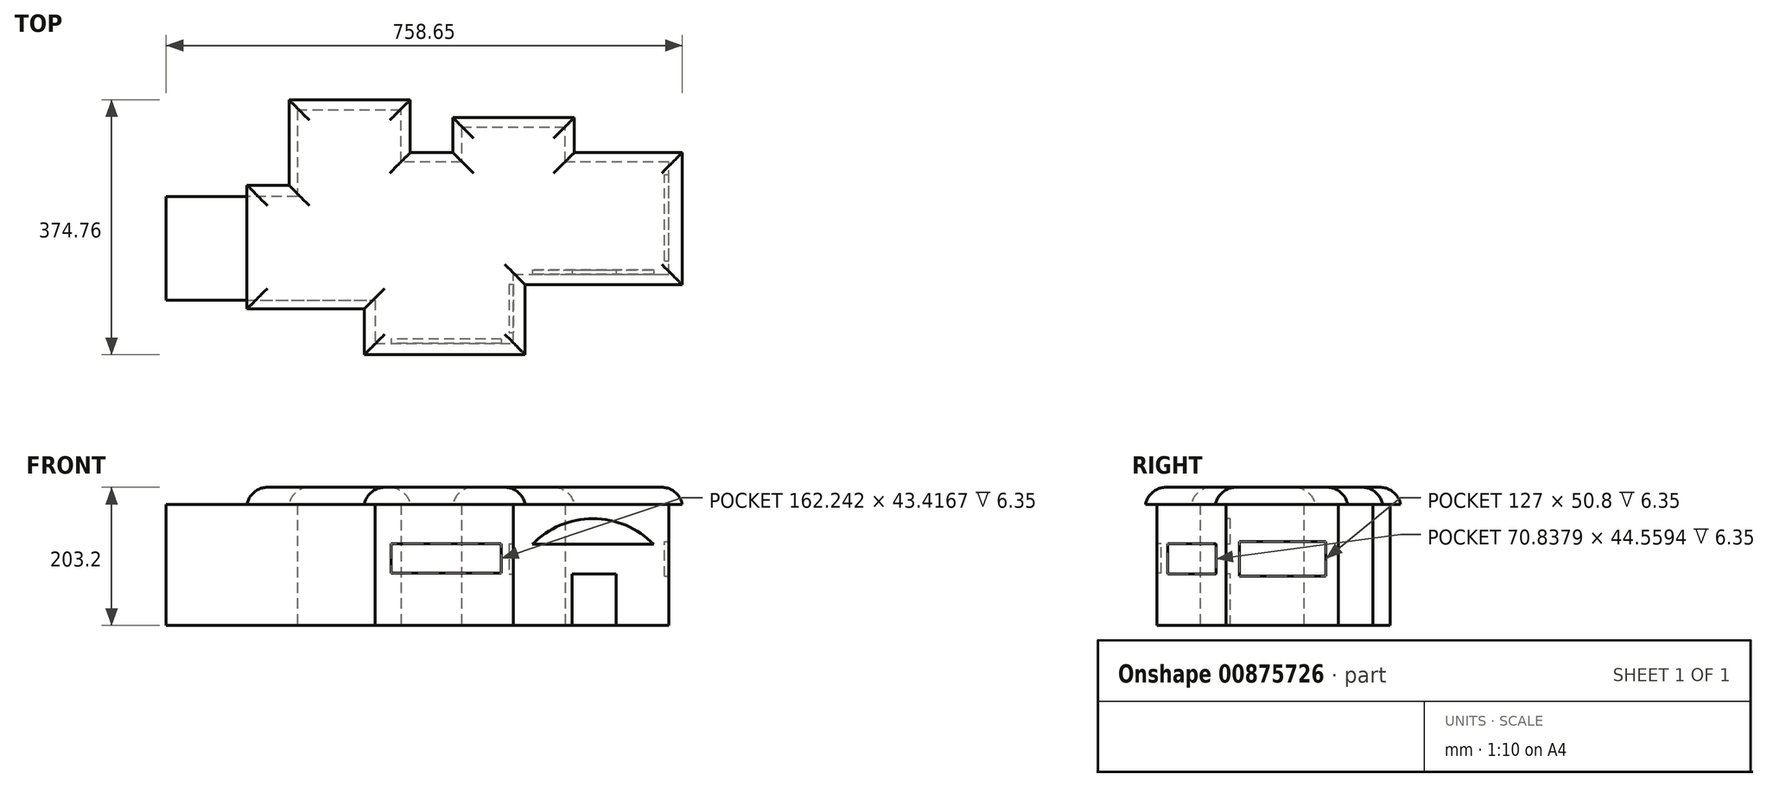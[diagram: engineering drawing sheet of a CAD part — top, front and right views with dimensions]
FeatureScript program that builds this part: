
annotation { "Feature Type Name" : "Feature", "Feature Type Description" : "" }
export const myFeature = defineFeature(function(context is Context, id is Id, definition is map)
    precondition{}
    {
        {
            var Q0;
            Q0=qCreatedBy(makeId("Top.planeOp"),FACE);
            var sketch = newSketch(context, id + "F0", { "sketchPlane" : qUnion([Q0])});
            skLineSegment(sketch, "E0", {"start": v(285.95, -165.1) * mm, "end": v(285.95, 0) * mm});
            skLineSegment(sketch, "E1", {"start": v(285.95, 0) * mm, "end": v(133.55, 0) * mm});
            skLineSegment(sketch, "E2", {"start": v(133.55, 0) * mm, "end": v(133.55, 50.8) * mm});
            skLineSegment(sketch, "E3", {"start": v(133.55, 50.8) * mm, "end": v(-18.85, 50.8) * mm});
            skLineSegment(sketch, "E4", {"start": v(-18.85, 50.8) * mm, "end": v(-18.85, 0) * mm});
            skLineSegment(sketch, "E5", {"start": v(-18.85, 0) * mm, "end": v(-107.75, 0) * mm});
            skLineSegment(sketch, "E6", {"start": v(-107.75, 0) * mm, "end": v(-107.75, 76.2) * mm});
            skLineSegment(sketch, "E7", {"start": v(-107.75, 76.2) * mm, "end": v(-260.15, 76.2) * mm});
            skLineSegment(sketch, "E8", {"start": v(-260.15, 76.2) * mm, "end": v(-260.15, -50.8) * mm});
            skLineSegment(sketch, "E9", {"start": v(-260.15, -50.8) * mm, "end": v(-310.95, -50.8) * mm});
            skLineSegment(sketch, "E10", {"start": v(-310.95, -50.8) * mm, "end": v(-310.95, -203.2) * mm});
            skLineSegment(sketch, "E11", {"start": v(-310.95, -203.2) * mm, "end": v(-145.85, -203.2) * mm});
            skLineSegment(sketch, "E12", {"start": v(-145.85, -203.2) * mm, "end": v(-145.85, -266.7) * mm});
            skLineSegment(sketch, "E13", {"start": v(-145.85, -266.7) * mm, "end": v(57.35, -266.7) * mm});
            skLineSegment(sketch, "E14", {"start": v(57.35, -266.7) * mm, "end": v(57.35, -165.1) * mm});
            skLineSegment(sketch, "E15", {"start": v(57.35, -165.1) * mm, "end": v(285.95, -165.1) * mm});
            skSolve(sketch);
        }
        {
            var Q0;
            Q0 = qSketchRegion(id + "F0", true);
            extrude(context, id + "F1", {"entities" : qUnion([Q0]), "depth" : 177.8 * mm, "offsetDistance" : 25.4 * mm});
        }
        {
            var Q0;
            Q0=makeQuery(id+"F1.opExtrude","SWEPT_FACE",FACE,{"disambiguationData":[OSD([sQuery(id+"F0.wireOp",EDGE,"E15")])]});
            var sketch = newSketch(context, id + "F2", { "sketchPlane" : qUnion([Q0])});
            skLineSegment(sketch, "E16", {"start": v(143.66, 0) * mm, "end": v(143.66, 75.76) * mm});
            skLineSegment(sketch, "E17", {"start": v(143.66, 75.76) * mm, "end": v(208.79, 75.76) * mm});
            skLineSegment(sketch, "E18", {"start": v(208.79, 75.76) * mm, "end": v(208.79, 0) * mm});
            skLineSegment(sketch, "E19", {"start": v(208.79, 0) * mm, "end": v(143.66, 0) * mm});
            skSolve(sketch);
        }
        {
            var Q0;
            Q0 = qSketchRegion(id + "F2", true);
            extrude(context, id + "F3", {"entities" : qUnion([Q0]), "operationType" : NewBodyOperationType.REMOVE, "oppositeDirection" : true, "depth" : 6.35 * mm, "offsetDistance" : 25.4 * mm});
        }
        {
            var Q0;
            Q0=makeQuery(id+"F1.opExtrude","SWEPT_FACE",FACE,{"disambiguationData":[OSD([sQuery(id+"F0.wireOp",EDGE,"E15")])]});
            var sketch = newSketch(context, id + "F4", { "sketchPlane" : qUnion([Q0])});
            skLineSegment(sketch, "E20", {"start": v(85.4, 119.18) * mm, "end": v(263.63, 119.18) * mm});
            skArc(sketch, "E21", {"start": v(263.63, 119.18) * mm, "mid": v(174.51, 156.97) * mm, "end": v(85.4, 119.18) * mm});
            skSolve(sketch);
        }
        {
            var Q0;
            Q0=makeQuery(id+"F4.imprint","IMPRINT",FACE,{"disambiguationData":[TD([[makeQuery(id+"F4.imprint","IMPRINT",EDGE,{"derivedFrom":sQuery(id+"F4.wireOp",EDGE,"E20")}),1.0]])]});
            extrude(context, id + "F5", {"entities" : qUnion([Q0]), "operationType" : NewBodyOperationType.REMOVE, "oppositeDirection" : true, "depth" : 6.35 * mm, "offsetDistance" : 25.4 * mm});
        }
        {
            var Q0;
            Q0=makeQuery(id+"F1.opExtrude","SWEPT_FACE",FACE,{"disambiguationData":[OSD([sQuery(id+"F0.wireOp",EDGE,"E0")])]});
            var sketch = newSketch(context, id + "F6", { "sketchPlane" : qUnion([Q0])});
            skLineSegment(sketch, "E22", {"start": v(-145.52, 123.15) * mm, "end": v(-18.52, 123.15) * mm});
            skLineSegment(sketch, "E23", {"start": v(-18.52, 123.15) * mm, "end": v(-18.52, 72.35) * mm});
            skLineSegment(sketch, "E24", {"start": v(-18.52, 72.35) * mm, "end": v(-145.52, 72.35) * mm});
            skLineSegment(sketch, "E25", {"start": v(-145.52, 72.35) * mm, "end": v(-145.52, 123.15) * mm});
            skSolve(sketch);
        }
        {
            var Q0;
            Q0=makeQuery(id+"F6.imprint","IMPRINT",FACE,{"disambiguationData":[TD([[makeQuery(id+"F6.imprint","IMPRINT",EDGE,{"derivedFrom":sQuery(id+"F6.wireOp",EDGE,"E22")}),-1.0]])]});
            extrude(context, id + "F7", {"entities" : qUnion([Q0]), "operationType" : NewBodyOperationType.REMOVE, "oppositeDirection" : true, "depth" : 6.35 * mm, "offsetDistance" : 25.4 * mm});
        }
        {
            var Q0;
            Q0=makeQuery(id+"F1.opExtrude","CAP_FACE",FACE,{"disambiguationData":[OSD([sQuery(id+"F0.wireOp",EDGE,"E0"),sQuery(id+"F0.wireOp",EDGE,"E1"),sQuery(id+"F0.wireOp",EDGE,"E2"),sQuery(id+"F0.wireOp",EDGE,"E3"),sQuery(id+"F0.wireOp",EDGE,"E4"),sQuery(id+"F0.wireOp",EDGE,"E5"),sQuery(id+"F0.wireOp",EDGE,"E6"),sQuery(id+"F0.wireOp",EDGE,"E7"),sQuery(id+"F0.wireOp",EDGE,"E8"),sQuery(id+"F0.wireOp",EDGE,"E9"),sQuery(id+"F0.wireOp",EDGE,"E10"),sQuery(id+"F0.wireOp",EDGE,"E11"),sQuery(id+"F0.wireOp",EDGE,"E12"),sQuery(id+"F0.wireOp",EDGE,"E13"),sQuery(id+"F0.wireOp",EDGE,"E14"),sQuery(id+"F0.wireOp",EDGE,"E15")])],"isStart":false});
            var sketch = newSketch(context, id + "F8", { "sketchPlane" : qUnion([Q0])});
            skLineSegment(sketch, "E26", {"start": v(-334.12, -34.28) * mm, "end": v(-334.12, -215.95) * mm});
            skLineSegment(sketch, "E27", {"start": v(-334.12, -215.95) * mm, "end": v(-161.6, -215.95) * mm});
            skLineSegment(sketch, "E28", {"start": v(-161.6, -215.95) * mm, "end": v(-161.6, -283.36) * mm});
            skLineSegment(sketch, "E29", {"start": v(-161.6, -283.36) * mm, "end": v(74.9, -283.36) * mm});
            skLineSegment(sketch, "E30", {"start": v(74.9, -283.36) * mm, "end": v(74.9, -180.53) * mm});
            skLineSegment(sketch, "E31", {"start": v(74.9, -180.53) * mm, "end": v(305.7, -180.53) * mm});
            skLineSegment(sketch, "E32", {"start": v(305.7, -180.53) * mm, "end": v(305.7, 13.7) * mm});
            skLineSegment(sketch, "E33", {"start": v(305.7, 13.7) * mm, "end": v(146.9, 13.7) * mm});
            skLineSegment(sketch, "E34", {"start": v(146.9, 13.7) * mm, "end": v(146.9, 65.12) * mm});
            skLineSegment(sketch, "E35", {"start": v(146.9, 65.12) * mm, "end": v(-31.35, 65.12) * mm});
            skLineSegment(sketch, "E36", {"start": v(-31.35, 65.12) * mm, "end": v(-31.35, 13.7) * mm});
            skLineSegment(sketch, "E37", {"start": v(-31.35, 13.7) * mm, "end": v(-94.19, 13.7) * mm});
            skLineSegment(sketch, "E38", {"start": v(-94.19, 13.7) * mm, "end": v(-94.19, 91.4) * mm});
            skLineSegment(sketch, "E39", {"start": v(-94.19, 91.4) * mm, "end": v(-272.42, 91.4) * mm});
            skLineSegment(sketch, "E40", {"start": v(-272.42, 91.4) * mm, "end": v(-272.42, -34.28) * mm});
            skLineSegment(sketch, "E41", {"start": v(-272.42, -34.28) * mm, "end": v(-334.12, -34.28) * mm});
            skSolve(sketch);
        }
        {
            var Q0;
            Q0 = qSketchRegion(id + "F8", true);
            extrude(context, id + "F9", {"entities" : qUnion([Q0]), "operationType" : NewBodyOperationType.ADD, "depth" : 25.4 * mm, "offsetDistance" : 25.4 * mm});
        }
        {
            var Q0;
            Q0=makeQuery(id+"F9.opExtrude","CAP_FACE",FACE,{"disambiguationData":[OSD([sQuery(id+"F8.wireOp",EDGE,"E26"),sQuery(id+"F8.wireOp",EDGE,"E27"),sQuery(id+"F8.wireOp",EDGE,"E28"),sQuery(id+"F8.wireOp",EDGE,"E29"),sQuery(id+"F8.wireOp",EDGE,"E30"),sQuery(id+"F8.wireOp",EDGE,"E31"),sQuery(id+"F8.wireOp",EDGE,"E32"),sQuery(id+"F8.wireOp",EDGE,"E33"),sQuery(id+"F8.wireOp",EDGE,"E34"),sQuery(id+"F8.wireOp",EDGE,"E35"),sQuery(id+"F8.wireOp",EDGE,"E36"),sQuery(id+"F8.wireOp",EDGE,"E37"),sQuery(id+"F8.wireOp",EDGE,"E38"),sQuery(id+"F8.wireOp",EDGE,"E39"),sQuery(id+"F8.wireOp",EDGE,"E40"),sQuery(id+"F8.wireOp",EDGE,"E41")])],"isStart":false});
            fillet(context, id + "F10", {"entities" : qUnion([Q0]), "radius" : 30.48 * mm, "tangentPropagation" : true, "allowEdgeOverflow" : false});
        }
        {
            var Q0;
            Q0=makeQuery(id+"F1.opExtrude","CAP_FACE",FACE,{"disambiguationData":[OSD([sQuery(id+"F0.wireOp",EDGE,"E0"),sQuery(id+"F0.wireOp",EDGE,"E1"),sQuery(id+"F0.wireOp",EDGE,"E2"),sQuery(id+"F0.wireOp",EDGE,"E3"),sQuery(id+"F0.wireOp",EDGE,"E4"),sQuery(id+"F0.wireOp",EDGE,"E5"),sQuery(id+"F0.wireOp",EDGE,"E6"),sQuery(id+"F0.wireOp",EDGE,"E7"),sQuery(id+"F0.wireOp",EDGE,"E8"),sQuery(id+"F0.wireOp",EDGE,"E9"),sQuery(id+"F0.wireOp",EDGE,"E10"),sQuery(id+"F0.wireOp",EDGE,"E11"),sQuery(id+"F0.wireOp",EDGE,"E12"),sQuery(id+"F0.wireOp",EDGE,"E13"),sQuery(id+"F0.wireOp",EDGE,"E14"),sQuery(id+"F0.wireOp",EDGE,"E15")])],"isStart":true});
            var sketch = newSketch(context, id + "F11", { "sketchPlane" : qUnion([Q0])});
            skLineSegment(sketch, "E42", {"start": v(-310.95, 203.2) * mm, "end": v(-452.95, 203.2) * mm});
            skLineSegment(sketch, "E43", {"start": v(-452.95, 203.2) * mm, "end": v(-452.95, 50.8) * mm});
            skLineSegment(sketch, "E44", {"start": v(-452.95, 50.8) * mm, "end": v(-310.95, 50.8) * mm});
            skLineSegment(sketch, "E45", {"start": v(-310.95, 50.8) * mm, "end": v(-310.95, 203.2) * mm});
            skSolve(sketch);
        }
        {
            var Q0;
            Q0 = qSketchRegion(id + "F11", true);
            extrude(context, id + "F12", {"entities" : qUnion([Q0]), "operationType" : NewBodyOperationType.ADD, "oppositeDirection" : true, "depth" : 177.8 * mm, "offsetDistance" : 25.4 * mm});
        }
        {
            var Q0;
            Q0=makeQuery(id+"F1.opExtrude","SWEPT_FACE",FACE,{"disambiguationData":[OSD([sQuery(id+"F0.wireOp",EDGE,"E13")])]});
            var sketch = newSketch(context, id + "F13", { "sketchPlane" : qUnion([Q0])});
            skLineSegment(sketch, "E46", {"start": v(39.73, 120.32) * mm, "end": v(-122.5, 120.32) * mm});
            skLineSegment(sketch, "E47", {"start": v(-122.5, 120.32) * mm, "end": v(-122.5, 76.9) * mm});
            skLineSegment(sketch, "E48", {"start": v(-122.5, 76.9) * mm, "end": v(39.73, 76.9) * mm});
            skLineSegment(sketch, "E49", {"start": v(39.73, 76.9) * mm, "end": v(39.73, 120.32) * mm});
            skSolve(sketch);
        }
        {
            var Q0;
            Q0=makeQuery(id+"F13.imprint","IMPRINT",FACE,{"disambiguationData":[TD([[makeQuery(id+"F13.imprint","IMPRINT",EDGE,{"derivedFrom":sQuery(id+"F13.wireOp",EDGE,"E46")}),1.0]])]});
            extrude(context, id + "F14", {"entities" : qUnion([Q0]), "operationType" : NewBodyOperationType.REMOVE, "oppositeDirection" : true, "depth" : 6.35 * mm, "offsetDistance" : 25.4 * mm});
        }
        {
            var Q0;
            Q0=makeQuery(id+"F1.opExtrude","SWEPT_FACE",FACE,{"disambiguationData":[OSD([sQuery(id+"F0.wireOp",EDGE,"E14")])]});
            var sketch = newSketch(context, id + "F15", { "sketchPlane" : qUnion([Q0])});
            skLineSegment(sketch, "E50", {"start": v(-179.9, 75.76) * mm, "end": v(-250.75, 75.76) * mm});
            skLineSegment(sketch, "E51", {"start": v(-250.75, 75.76) * mm, "end": v(-250.75, 120.32) * mm});
            skLineSegment(sketch, "E52", {"start": v(-250.75, 120.32) * mm, "end": v(-179.9, 120.32) * mm});
            skLineSegment(sketch, "E53", {"start": v(-179.9, 120.32) * mm, "end": v(-179.9, 75.76) * mm});
            skSolve(sketch);
        }
        {
            var Q0;
            Q0=makeQuery(id+"F15.imprint","IMPRINT",FACE,{"disambiguationData":[TD([[makeQuery(id+"F15.imprint","IMPRINT",EDGE,{"derivedFrom":sQuery(id+"F15.wireOp",EDGE,"E50")}),-1.0]])]});
            extrude(context, id + "F16", {"entities" : qUnion([Q0]), "operationType" : NewBodyOperationType.REMOVE, "oppositeDirection" : true, "depth" : 6.35 * mm, "offsetDistance" : 25.4 * mm});
        }
    });
